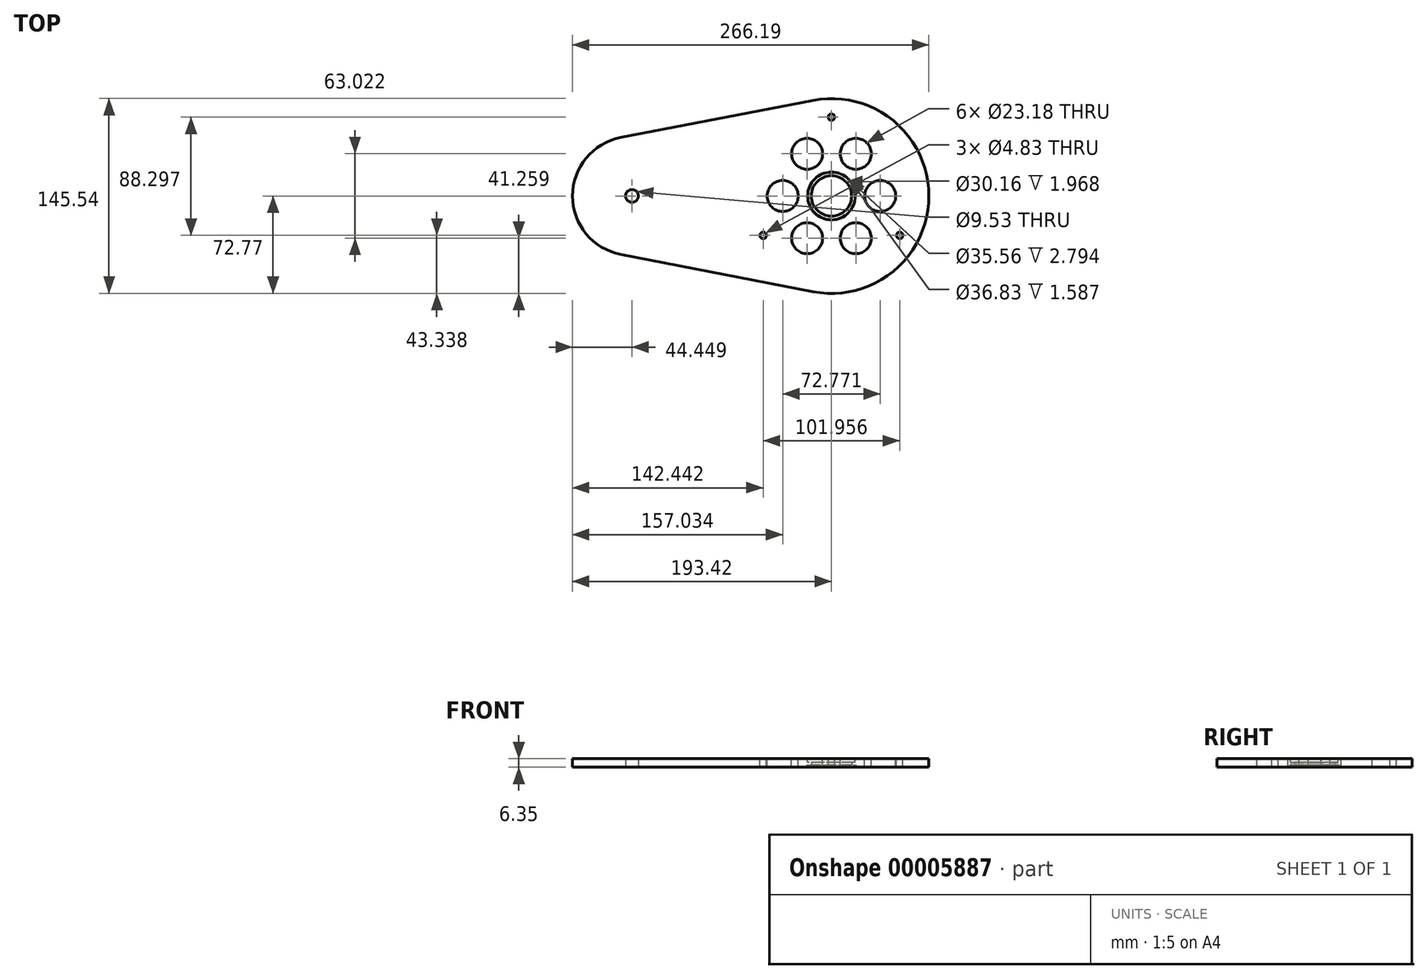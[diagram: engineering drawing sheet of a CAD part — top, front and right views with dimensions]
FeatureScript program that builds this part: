
annotation { "Feature Type Name" : "Feature", "Feature Type Description" : "" }
export const myFeature = defineFeature(function(context is Context, id is Id, definition is map)
    precondition{}
    {
        {
            var Q0;
            Q0=qCreatedBy(makeId("Top.planeOp"),FACE);
            var sketch = newSketch(context, id + "F0", { "sketchPlane" : qUnion([Q0])});
            skArc(sketch, "E0", {"start": v(-13.83, -71.44) * mm, "mid": v(72.77, 0) * mm, "end": v(-13.83, 71.44) * mm});
            skCircle(sketch, "E1", {"center": v(0, 0) * mm, "radius": 15.08 * mm});
            skLineSegment(sketch, "E2", {"start": v(0, 0) * mm, "end": v(-72.77, 0) * mm, "construction": true});
            skLineSegment(sketch, "E3", {"start": v(-72.77, 0) * mm, "end": v(-148.97, 0) * mm, "construction": true});
            skArc(sketch, "E4", {"start": v(-157.42, 43.64) * mm, "mid": v(-193.42, 0) * mm, "end": v(-157.42, -43.64) * mm});
            skLineSegment(sketch, "E5", {"start": v(-157.42, 43.64) * mm, "end": v(-13.83, 71.44) * mm});
            skLineSegment(sketch, "E6", {"start": v(-157.42, -43.64) * mm, "end": v(-13.83, -71.44) * mm});
            skCircle(sketch, "E7", {"center": v(-148.97, 0) * mm, "radius": 4.76 * mm});
            skSolve(sketch);
        }
        {
            var Q0;
            Q0=makeQuery(id+"F0.imprint","IMPRINT",FACE,{"disambiguationData":[TD([[makeQuery(id+"F0.imprint","IMPRINT",EDGE,{"derivedFrom":sQuery(id+"F0.wireOp",EDGE,"E0")}),1.0]])]});
            extrude(context, id + "F1", {"entities" : qUnion([Q0]), "depth" : 6.35 * mm});
        }
        {
            var Q0;
            Q0=makeQuery(id+"F1.opExtrude","CAP_FACE",FACE,{"disambiguationData":[OSD([sQuery(id+"F0.wireOp",EDGE,"E0"),sQuery(id+"F0.wireOp",EDGE,"E1"),sQuery(id+"F0.wireOp",EDGE,"7409aa68-249a-4d23-94e3-a1b410b62b42")])],"isStart":false});
            var sketch = newSketch(context, id + "F2", { "sketchPlane" : qUnion([Q0])});
            skLineSegment(sketch, "E8", {"start": v(0, 0) * mm, "end": v(0, 72.77) * mm, "construction": true});
            skCircle(sketch, "E9", {"center": v(0, 58.86) * mm, "radius": 4.76 * mm});
            skCircle(sketch, "E10.1.0", {"center": v(-50.98, -29.43) * mm, "radius": 4.76 * mm});
            skCircle(sketch, "E10.2.0", {"center": v(50.98, -29.43) * mm, "radius": 4.76 * mm});
            skPoint(sketch, "E10.center", {"position": v(0, 0) * mm});
            skCircle(sketch, "E11", {"center": v(0, 58.86) * mm, "radius": 2.41 * mm});
            skCircle(sketch, "E12.1.0", {"center": v(-50.98, -29.43) * mm, "radius": 2.41 * mm});
            skCircle(sketch, "E12.2.0", {"center": v(50.98, -29.43) * mm, "radius": 2.41 * mm});
            skSolve(sketch);
        }
        {
            var Q0;
            Q0=makeQuery(id+"F2.imprint","IMPRINT",FACE,{"disambiguationData":[TD([[makeQuery(id+"F2.imprint","IMPRINT",EDGE,{"derivedFrom":sQuery(id+"F2.wireOp",EDGE,"E12.1.0")}),1.0]])]});
            var Q1;
            Q1=makeQuery(id+"F2.imprint","IMPRINT",FACE,{"disambiguationData":[TD([[makeQuery(id+"F2.imprint","IMPRINT",EDGE,{"derivedFrom":sQuery(id+"F2.wireOp",EDGE,"E12.2.0")}),1.0]])]});
            var Q2;
            Q2=makeQuery(id+"F2.imprint","IMPRINT",FACE,{"disambiguationData":[TD([[makeQuery(id+"F2.imprint","IMPRINT",EDGE,{"derivedFrom":sQuery(id+"F2.wireOp",EDGE,"E11")}),1.0]])]});
            extrude(context, id + "F3", {"entities" : qUnion([Q0, Q1, Q2]), "operationType" : NewBodyOperationType.REMOVE, "endBound" : BoundingType.THROUGH_ALL, "oppositeDirection" : true, "depth" : 25.4 * mm});
        }
        {
            var Q0;
            Q0=makeQuery(id+"F1.opExtrude","CAP_FACE",FACE,{"disambiguationData":[OSD([sQuery(id+"F0.wireOp",EDGE,"E0"),sQuery(id+"F0.wireOp",EDGE,"E1"),sQuery(id+"F0.wireOp",EDGE,"7409aa68-249a-4d23-94e3-a1b410b62b42")])],"isStart":false});
            var sketch = newSketch(context, id + "F4", { "sketchPlane" : qUnion([Q0])});
            skCircle(sketch, "E13", {"center": v(0, 0) * mm, "radius": 17.78 * mm});
            skSolve(sketch);
        }
        {
            var Q0;
            Q0=makeQuery(id+"F4.imprint","IMPRINT",FACE,{"disambiguationData":[TD([[makeQuery(id+"F4.imprint","IMPRINT",EDGE,{"derivedFrom":sQuery(id+"F4.wireOp",EDGE,"E13")}),1.0]])]});
            extrude(context, id + "F5", {"entities" : qUnion([Q0]), "operationType" : NewBodyOperationType.REMOVE, "oppositeDirection" : true, "depth" : 2.8 * mm});
        }
        {
            var Q0;
            Q0=makeQuery(id+"F1.opExtrude","CAP_FACE",FACE,{"disambiguationData":[OSD([sQuery(id+"F0.wireOp",EDGE,"E0"),sQuery(id+"F0.wireOp",EDGE,"E1"),sQuery(id+"F0.wireOp",EDGE,"7409aa68-249a-4d23-94e3-a1b410b62b42")])],"isStart":true});
            var sketch = newSketch(context, id + "F6", { "sketchPlane" : qUnion([Q0])});
            skCircle(sketch, "E14", {"center": v(0, 0) * mm, "radius": 18.41 * mm});
            skSolve(sketch);
        }
        {
            var Q0;
            Q0=makeQuery(id+"F6.imprint","IMPRINT",FACE,{"disambiguationData":[TD([[makeQuery(id+"F6.imprint","IMPRINT",EDGE,{"derivedFrom":sQuery(id+"F6.wireOp",EDGE,"E14")}),1.0]])]});
            extrude(context, id + "F7", {"entities" : qUnion([Q0]), "operationType" : NewBodyOperationType.REMOVE, "oppositeDirection" : true, "depth" : 1.59 * mm});
        }
        {
            var Q0;
            Q0=makeQuery(id+"F1.opExtrude","CAP_FACE",FACE,{"disambiguationData":[OSD([sQuery(id+"F0.wireOp",EDGE,"E0"),sQuery(id+"F0.wireOp",EDGE,"E1")])],"isStart":false});
            var sketch = newSketch(context, id + "F8", { "sketchPlane" : qUnion([Q0])});
            skLineSegment(sketch, "E15", {"start": v(0, 0) * mm, "end": v(-72.77, 0) * mm, "construction": true});
            skCircle(sketch, "E16", {"center": v(-36.39, 0) * mm, "radius": 11.59 * mm});
            skCircle(sketch, "E17.1.0", {"center": v(-18.2, -31.51) * mm, "radius": 11.59 * mm});
            skCircle(sketch, "E17.2.0", {"center": v(18.2, -31.51) * mm, "radius": 11.59 * mm});
            skCircle(sketch, "E17.3.0", {"center": v(36.39, 0) * mm, "radius": 11.59 * mm});
            skCircle(sketch, "E17.4.0", {"center": v(18.2, 31.51) * mm, "radius": 11.59 * mm});
            skCircle(sketch, "E17.5.0", {"center": v(-18.2, 31.51) * mm, "radius": 11.59 * mm});
            skPoint(sketch, "E17.center", {"position": v(0, 0) * mm});
            skSolve(sketch);
        }
        {
            var Q0;
            Q0 = qSketchRegion(id + "F8", true);
            extrude(context, id + "F9", {"entities" : qUnion([Q0]), "operationType" : NewBodyOperationType.REMOVE, "endBound" : BoundingType.THROUGH_ALL, "oppositeDirection" : true, "depth" : 25.4 * mm});
        }
    });
